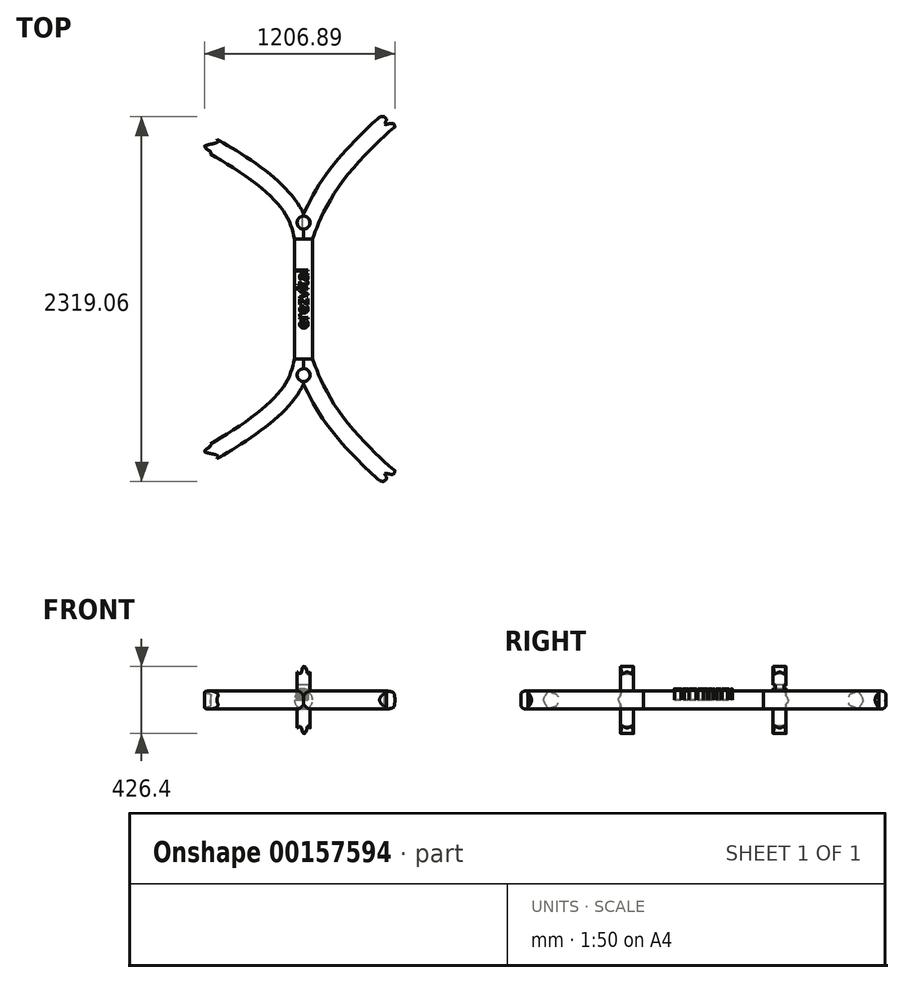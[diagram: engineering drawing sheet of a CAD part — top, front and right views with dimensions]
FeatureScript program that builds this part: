
annotation { "Feature Type Name" : "Feature", "Feature Type Description" : "" }
export const myFeature = defineFeature(function(context is Context, id is Id, definition is map)
    precondition{}
    {
        {
            var Q0;
            Q0=qCreatedBy(makeId("Front.planeOp"),FACE);
            var sketch = newSketch(context, id + "F0", { "sketchPlane" : qUnion([Q0])});
            skArc(sketch, "E0", {"start": v(57.52, 0) * mm, "mid": v(0, 57.52) * mm, "end": v(-57.52, 0) * mm});
            skLineSegment(sketch, "E1", {"start": v(-57.52, 0) * mm, "end": v(57.52, 0) * mm});
            skFitSpline(sketch, "E2", {"points": [v(-91.95, 213.06) * mm, v(-19.19, 170.9) * mm, v(0, 212.18) * mm, v(19.72, 187.58) * mm, v(50.02, 194.43) * mm], "startDerivative": vector(450.56, -249.8) * mm, "endDerivative": vector(352.26, 732.01) * mm});
            skLineSegment(sketch, "E3", {"start": v(50.02, 194.43) * mm, "end": v(50.02, 489.41) * mm});
            skLineSegment(sketch, "E4", {"start": v(50.02, 489.41) * mm, "end": v(-91.95, 489.41) * mm});
            skLineSegment(sketch, "E5", {"start": v(-91.95, 489.41) * mm, "end": v(-91.95, 213.06) * mm});
            skSolve(sketch);
        }
        {
            var Q0;
            Q0=qCreatedBy(makeId("Top.planeOp"),FACE);
            var sketch = newSketch(context, id + "F13", { "sketchPlane" : qUnion([Q0])});
            skFitSpline(sketch, "E6", {"points": [v(0, 0) * mm, v(172.63, -355.58) * mm, v(547.22, -755.1) * mm], "startDerivative": vector(56.7, -196.86) * mm, "endDerivative": vector(174.2, -124.4) * mm});
            skFitSpline(sketch, "E7", {"points": [v(0, 0) * mm, v(-45.9, -134.8) * mm, v(-278.86, -396.21) * mm, v(-628.42, -614.2) * mm], "startDerivative": vector(-167.38, -324.71) * mm, "endDerivative": vector(-385.6, -149.77) * mm});
            skCircle(sketch, "E8", {"center": v(0, -103.28) * mm, "radius": 41.3 * mm});
            skFitSpline(sketch, "E9", {"points": [v(-651.54, -524.64) * mm, v(-588.57, -548.86) * mm, v(-627.36, -588.2) * mm, v(-543.98, -617.28) * mm, v(-563.63, -650.35) * mm, v(-482.27, -668.8) * mm], "startDerivative": vector(505.2, -84.26) * mm, "endDerivative": vector(558.51, -31.46) * mm});
            skLineSegment(sketch, "E10", {"start": v(-482.27, -668.8) * mm, "end": v(-762.28, -841.62) * mm});
            skLineSegment(sketch, "E11", {"start": v(-762.28, -841.62) * mm, "end": v(-872.88, -662.44) * mm});
            skLineSegment(sketch, "E12", {"start": v(-872.88, -662.44) * mm, "end": v(-651.54, -524.64) * mm});
            skFitSpline(sketch, "E13", {"points": [v(476.24, -771.62) * mm, v(515.82, -772.4) * mm, v(527.16, -757.17) * mm, v(515.82, -727.8) * mm, v(568.73, -732.68) * mm, v(579.83, -676.18) * mm, v(635.14, -605.02) * mm], "startDerivative": vector(723.8, -225.08) * mm, "endDerivative": vector(493.18, 342.04) * mm});
            skLineSegment(sketch, "E14", {"start": v(635.14, -605.02) * mm, "end": v(870.77, -795.08) * mm});
            skLineSegment(sketch, "E15", {"start": v(870.77, -795.08) * mm, "end": v(628.33, -1027.2) * mm});
            skLineSegment(sketch, "E16", {"start": v(628.33, -1027.2) * mm, "end": v(476.24, -771.62) * mm});
            skSolve(sketch);
        }
        {
            var Q0;
            {var subQ0=sQuery(id+"F13.wireOp",EDGE,"E8");var subQ1=sQuery(id+"F13.wireOp",EDGE,"E6");var subQ2=makeQuery(id+"F13.imprint","INTERSECT",VERTEX,{"disambiguationData":[OD(0.0)],"derivedFrom":[subQ1,subQ0]});Q0=makeQuery(id+"F13.imprint","IMPRINT",FACE,{"disambiguationData":[TD([[makeQuery(id+"F13.imprint","IMPRINT",EDGE,{"disambiguationData":[TD([[subQ2,1.0]])],"derivedFrom":subQ1}),-1.0]])]});}
            var Q1;
            {var subQ0=sQuery(id+"F13.wireOp",EDGE,"E8");var subQ1=sQuery(id+"F13.wireOp",EDGE,"E6");var subQ2=makeQuery(id+"F13.imprint","INTERSECT",VERTEX,{"disambiguationData":[OD(0.0)],"derivedFrom":[subQ1,subQ0]});Q1=makeQuery(id+"F13.imprint","IMPRINT",FACE,{"disambiguationData":[TD([[makeQuery(id+"F13.imprint","IMPRINT",EDGE,{"disambiguationData":[TD([[subQ2,1.0]])],"derivedFrom":subQ1}),1.0]])]});}
            var Q2;
            {var subQ0=sQuery(id+"F13.wireOp",EDGE,"E8");var subQ1=sQuery(id+"F13.wireOp",EDGE,"E7");var subQ2=makeQuery(id+"F13.imprint","INTERSECT",VERTEX,{"disambiguationData":[OD(0.0)],"derivedFrom":[subQ1,subQ0]});Q2=makeQuery(id+"F13.imprint","IMPRINT",FACE,{"disambiguationData":[TD([[makeQuery(id+"F13.imprint","IMPRINT",EDGE,{"disambiguationData":[TD([[subQ2,1.0]])],"derivedFrom":subQ1}),-1.0]])]});}
            extrude(context, id + "F1", {"entities" : qUnion([Q0, Q1, Q2]), "depth" : 254 * mm});
        }
        {
            var Q0;
            Q0=makeQuery(id+"F0.imprint","IMPRINT",FACE,{"disambiguationData":[TD([[makeQuery(id+"F0.imprint","IMPRINT",EDGE,{"derivedFrom":sQuery(id+"F0.wireOp",EDGE,"E0")}),1.0]])]});
            var Q1;
            Q1=sQuery(id+"F13.wireOp",EDGE,"E7");
            sweep(context, id + "F2", {"operationType" : NewBodyOperationType.ADD, "profiles" : qUnion([Q0]), "path" : qUnion([Q1])});
        }
        {
            var Q0;
            Q0=makeQuery(id+"F0.imprint","IMPRINT",FACE,{"disambiguationData":[TD([[makeQuery(id+"F0.imprint","IMPRINT",EDGE,{"derivedFrom":sQuery(id+"F0.wireOp",EDGE,"E0")}),1.0]])]});
            var Q1;
            Q1=sQuery(id+"F13.wireOp",EDGE,"E6");
            sweep(context, id + "F14", {"operationType" : NewBodyOperationType.ADD, "profiles" : qUnion([Q0]), "path" : qUnion([Q1])});
        }
        {
            var Q0;
            Q0=makeQuery(id+"F0.imprint","IMPRINT",FACE,{"disambiguationData":[TD([[makeQuery(id+"F0.imprint","IMPRINT",EDGE,{"derivedFrom":sQuery(id+"F0.wireOp",EDGE,"E2")}),1.0]])]});
            extrude(context, id + "F3", {"entities" : qUnion([Q0]), "operationType" : NewBodyOperationType.REMOVE, "endBound" : BoundingType.THROUGH_ALL, "depth" : 25.4 * mm});
        }
        {
            var Q0;
            Q0=makeQuery(id+"F2.opSweep","CAP_FACE",FACE,{"disambiguationData":[OSD([sQuery(id+"F0.wireOp",EDGE,"E0"),sQuery(id+"F0.wireOp",EDGE,"E1"),sQuery(id+"F13.wireOp",VERTEX,"E7.start")])],"isStart":true});
            extrude(context, id + "F4", {"entities" : qUnion([Q0]), "operationType" : NewBodyOperationType.ADD, "depth" : 381 * mm});
        }
        {
            var Q0;
            {var subQ0=sQuery(id+"F13.wireOp",EDGE,"E14");Q0=makeQuery(id+"F13.imprint","IMPRINT",FACE,{"disambiguationData":[TD([[makeQuery(id+"F13.imprint","IMPRINT",EDGE,{"derivedFrom":subQ0}),-1.0]])]});}
            extrude(context, id + "F5", {"entities" : qUnion([Q0]), "operationType" : NewBodyOperationType.REMOVE, "endBound" : BoundingType.THROUGH_ALL, "depth" : 25.4 * mm});
        }
        {
            var Q0;
            {var subQ0=sQuery(id+"F13.wireOp",EDGE,"E10");Q0=makeQuery(id+"F13.imprint","IMPRINT",FACE,{"disambiguationData":[TD([[makeQuery(id+"F13.imprint","IMPRINT",EDGE,{"derivedFrom":subQ0}),-1.0]])]});}
            extrude(context, id + "F6", {"entities" : qUnion([Q0]), "operationType" : NewBodyOperationType.REMOVE, "endBound" : BoundingType.THROUGH_ALL, "depth" : 25.4 * mm});
        }
        {
            var Q0;
            Q0=makeQuery(id+"F1.opExtrude","SWEPT_BODY",BODY,{"disambiguationData":[OSD([sQuery(id+"F13.wireOp",EDGE,"E8")])]});
            var Q1;
            Q1=makeQuery(id+"F4.opExtrude","CAP_FACE",FACE,{"disambiguationData":[OSD([sQuery(id+"F0.wireOp",EDGE,"E0"),sQuery(id+"F0.wireOp",EDGE,"E1"),sQuery(id+"F13.wireOp",VERTEX,"E7.start")])],"isStart":false});
            mirror(context, id + "F7", {"operationType" : NewBodyOperationType.ADD, "entities" : qUnion([Q0]), "mirrorPlane" : qUnion([Q1])});
        }
        {
            var Q0;
            Q0=makeQuery(id+"F1.opExtrude","SWEPT_BODY",BODY,{"disambiguationData":[OSD([sQuery(id+"F13.wireOp",EDGE,"E8")])]});
            var Q1;
            {var subQ0=sQuery(id+"F0.wireOp",EDGE,"E1");var subQ1=makeQuery(id+"F4.boolean.opBoolean","MERGE",FACE,{"derivedFrom":[makeQuery(id+"F14.boolean.opBoolean","MERGE",FACE,{"derivedFrom":[makeQuery(id+"F2.boolean.opBoolean","MERGE",FACE,{"derivedFrom":[makeQuery(id+"F1.opExtrude","CAP_FACE",FACE,{"disambiguationData":[OSD([sQuery(id+"F13.wireOp",EDGE,"E8")])],"isStart":true}),makeQuery(id+"F2.opSweep","SWEPT_FACE",FACE,{"disambiguationData":[OSD([subQ0,sQuery(id+"F13.wireOp",EDGE,"E7")])]})]}),makeQuery(id+"F14.opSweep","SWEPT_FACE",FACE,{"disambiguationData":[OSD([subQ0,sQuery(id+"F13.wireOp",EDGE,"E6")])]})]}),makeQuery(id+"F4.opExtrude","SWEPT_FACE",FACE,{"disambiguationData":[OSD([subQ0,sQuery(id+"F13.wireOp",VERTEX,"E7.start")])]})]});Q1=makeQuery(id+"F7.boolean.opBoolean","MERGE",FACE,{"derivedFrom":[subQ1,makeQuery(id+"F7.opPattern","COPY",FACE,{"derivedFrom":subQ1,"instanceName":"1"})]});}
            mirror(context, id + "F15", {"operationType" : NewBodyOperationType.ADD, "entities" : qUnion([Q0]), "mirrorPlane" : qUnion([Q1])});
        }
        {
            var Q0;
            Q0=qCreatedBy(makeId("Top.planeOp"),FACE);
            var sketch = newSketch(context, id + "F8", { "sketchPlane" : qUnion([Q0])});
            skText(sketch, "E17", { "text": "erezvital", "fontName": "OpenSans-Regular.ttf"});
            const initialGuessF8  = {"E17": [0.0279, 0.1906, 0, 1, 0.07046]};
            skSetInitialGuess(sketch, initialGuessF8);
            skSolve(sketch);
        }
        {
            var Q0;
            Q0 = qSketchRegion(id + "F8", true);
            extrude(context, id + "F9", {"entities" : qUnion([Q0]), "depth" : 85.72 * mm});
        }
        {
            var Q0;
            Q0=qCreatedBy(makeId("Front.planeOp"),FACE);
            var sketch = newSketch(context, id + "F10", { "sketchPlane" : qUnion([Q0])});
            skLineSegment(sketch, "E18.0.1", {"start": v(27.9, 64.03) * mm, "end": v(27.9, 0) * mm});
            skLineSegment(sketch, "E18.0.3", {"start": v(-46.45, 0) * mm, "end": v(-46.45, 64.03) * mm});
            skLineSegment(sketch, "E19", {"start": v(-9.27, 0) * mm, "end": v(-9.27, 104.29) * mm, "construction": true});
            skFitSpline(sketch, "E20", {"points": [v(-9.14, 71.29) * mm, v(9.59, 68.39) * mm, v(31.67, 60.33) * mm, v(31.67, 60.2) * mm], "startDerivative": vector(35, -2.22) * mm, "endDerivative": vector(-1.7, -2.79) * mm});
            skLineSegment(sketch, "E21", {"start": v(31.67, 60.33) * mm, "end": v(31.67, 94.78) * mm});
            skLineSegment(sketch, "E22", {"start": v(31.67, 94.78) * mm, "end": v(-9.14, 94.78) * mm});
            skFitSpline(sketch, "E23.MirrorCS", {"points": [v(-9.14, 71.29) * mm, v(-27.88, 68.39) * mm, v(-49.96, 60.33) * mm, v(-49.96, 60.2) * mm], "startDerivative": vector(-35, -2.22) * mm, "endDerivative": vector(1.7, -2.79) * mm});
            skLineSegment(sketch, "E24.MirrorCS", {"start": v(-49.96, 60.33) * mm, "end": v(-49.96, 94.78) * mm});
            skLineSegment(sketch, "E25.MirrorCS", {"start": v(-49.96, 94.78) * mm, "end": v(-9.14, 94.78) * mm});
            skSolve(sketch);
        }
        {
            var Q0;
            {var subQ4=sQuery(id+"F10.wireOp",EDGE,"E21");Q0=makeQuery(id+"F10.imprint","IMPRINT",FACE,{"disambiguationData":[TD([[makeQuery(id+"F10.imprint","IMPRINT",EDGE,{"derivedFrom":subQ4}),1.0]])]});}
            extrude(context, id + "F11", {"entities" : qUnion([Q0]), "operationType" : NewBodyOperationType.REMOVE, "endBound" : BoundingType.THROUGH_ALL, "oppositeDirection" : true, "depth" : 25.4 * mm, "hasSecondDirection" : true, "secondDirectionOppositeDirection" : false, "secondDirectionDepth" : 25.4 * mm});
        }
        {
            var Q0;
            {var subQ4=sQuery(id+"F10.wireOp",EDGE,"E21");Q0=makeQuery(id+"F10.imprint","IMPRINT",FACE,{"disambiguationData":[TD([[makeQuery(id+"F10.imprint","IMPRINT",EDGE,{"derivedFrom":subQ4}),1.0]])]});}
            extrude(context, id + "F12", {"entities" : qUnion([Q0]), "operationType" : NewBodyOperationType.REMOVE, "endBound" : BoundingType.THROUGH_ALL, "oppositeDirection" : true, "depth" : 25.4 * mm});
        }
    });
